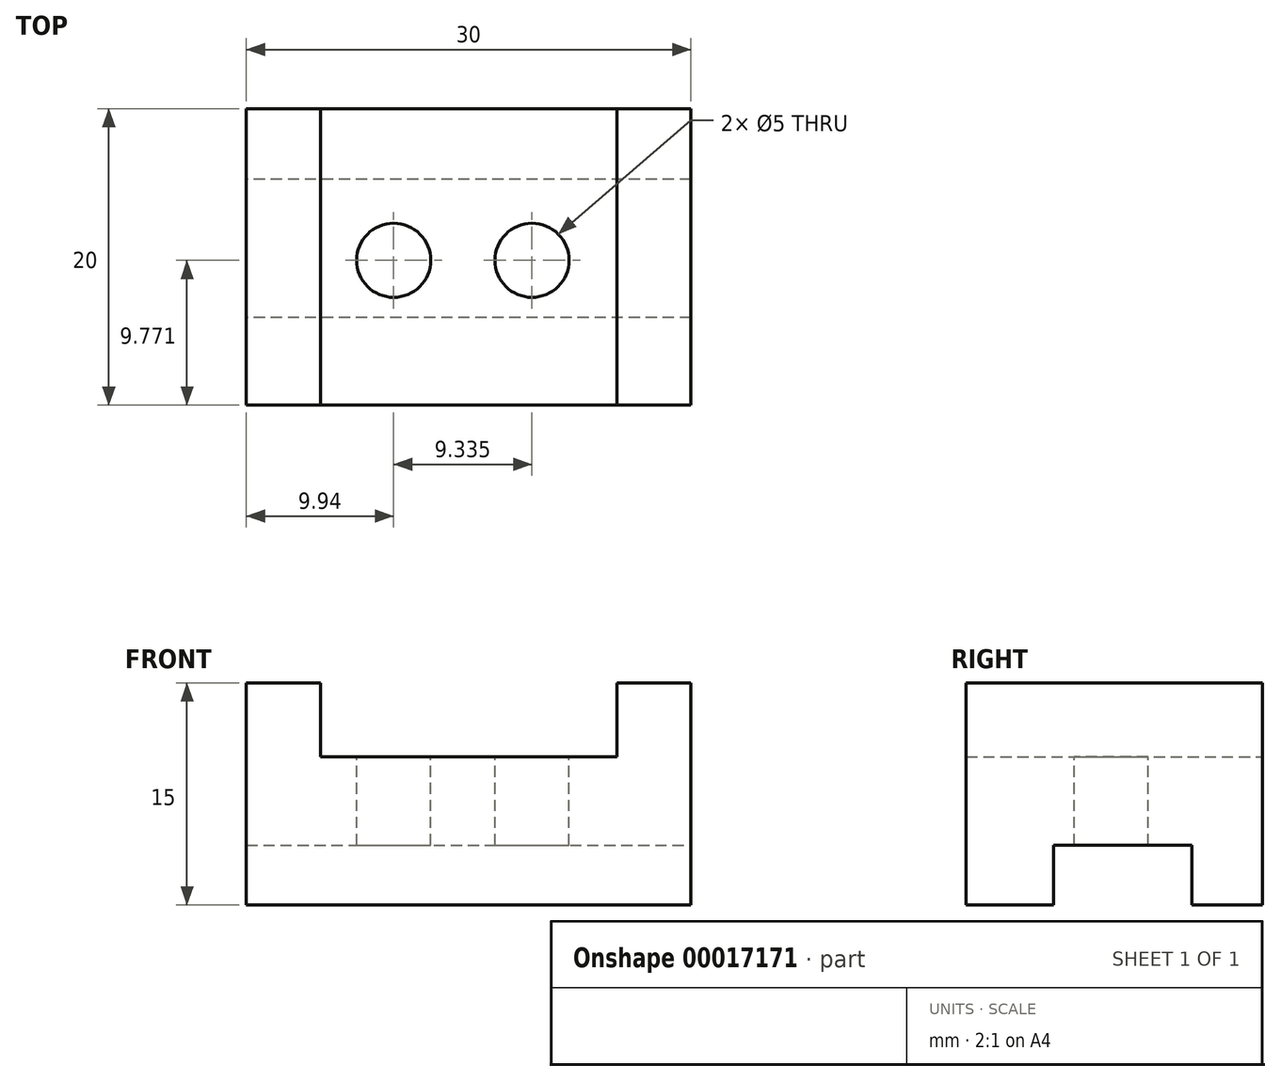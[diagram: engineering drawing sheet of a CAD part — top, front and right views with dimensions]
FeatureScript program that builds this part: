
annotation { "Feature Type Name" : "Feature", "Feature Type Description" : "" }
export const myFeature = defineFeature(function(context is Context, id is Id, definition is map)
    precondition{}
    {
        {
            var Q0;
            Q0=qCreatedBy(makeId("Front.planeOp"),FACE);
            var sketch = newSketch(context, id + "F0", { "sketchPlane" : qUnion([Q0])});
            skLineSegment(sketch, "E0.bottom", {"start": v(-30, -34.73) * mm, "end": v(0, -34.73) * mm});
            skLineSegment(sketch, "E0.top", {"start": v(-30, -19.73) * mm, "end": v(-25, -19.73) * mm});
            skLineSegment(sketch, "E0.left", {"start": v(-30, -34.73) * mm, "end": v(-30, -19.73) * mm});
            skLineSegment(sketch, "E0.right", {"start": v(0, -34.73) * mm, "end": v(0, -19.73) * mm});
            skLineSegment(sketch, "E1", {"start": v(-25, -24.73) * mm, "end": v(-5, -24.73) * mm});
            skLineSegment(sketch, "E2", {"start": v(-25, -19.73) * mm, "end": v(-25, -24.73) * mm});
            skLineSegment(sketch, "E3", {"start": v(-5, -19.73) * mm, "end": v(-5, -24.73) * mm});
            skLineSegment(sketch, "E4.trimOffspring", {"start": v(-5, -19.73) * mm, "end": v(0, -19.73) * mm});
            skPoint(sketch, "E5.orphan", {"position": v(0, -24.73) * mm});
            skSolve(sketch);
        }
        {
            var Q0;
            Q0 = qSketchRegion(id + "F0", true);
            extrude(context, id + "F1", {"entities" : qUnion([Q0]), "depth" : 20 * mm});
        }
        {
            var Q0;
            Q0=qCreatedBy(makeId("Top.planeOp"),FACE);
            var sketch = newSketch(context, id + "F2", { "sketchPlane" : qUnion([Q0])});
            skCircle(sketch, "E6", {"center": v(-20.06, -10.23) * mm, "radius": 2.5 * mm});
            skCircle(sketch, "E7", {"center": v(-10.73, -10.23) * mm, "radius": 2.5 * mm});
            skSolve(sketch);
        }
        {
            var Q0;
            Q0 = qSketchRegion(id + "F2", true);
            extrude(context, id + "F3", {"entities" : qUnion([Q0]), "operationType" : NewBodyOperationType.REMOVE, "endBound" : BoundingType.THROUGH_ALL, "oppositeDirection" : true, "depth" : 25 * mm});
        }
        {
            var Q0;
            Q0=qCreatedBy(makeId("Right.planeOp"),FACE);
            var sketch = newSketch(context, id + "F4", { "sketchPlane" : qUnion([Q0])});
            skLineSegment(sketch, "E8.bottom", {"start": v(-14.1, -34.86) * mm, "end": v(-4.77, -34.86) * mm});
            skLineSegment(sketch, "E8.top", {"start": v(-14.1, -30.69) * mm, "end": v(-4.77, -30.69) * mm});
            skLineSegment(sketch, "E8.left", {"start": v(-14.1, -34.86) * mm, "end": v(-14.1, -30.69) * mm});
            skLineSegment(sketch, "E8.right", {"start": v(-4.77, -34.86) * mm, "end": v(-4.77, -30.69) * mm});
            skSolve(sketch);
        }
        {
            var Q0;
            Q0 = qSketchRegion(id + "F4", true);
            extrude(context, id + "F5", {"entities" : qUnion([Q0]), "operationType" : NewBodyOperationType.REMOVE, "endBound" : BoundingType.THROUGH_ALL, "oppositeDirection" : true, "depth" : 25 * mm});
        }
    });
